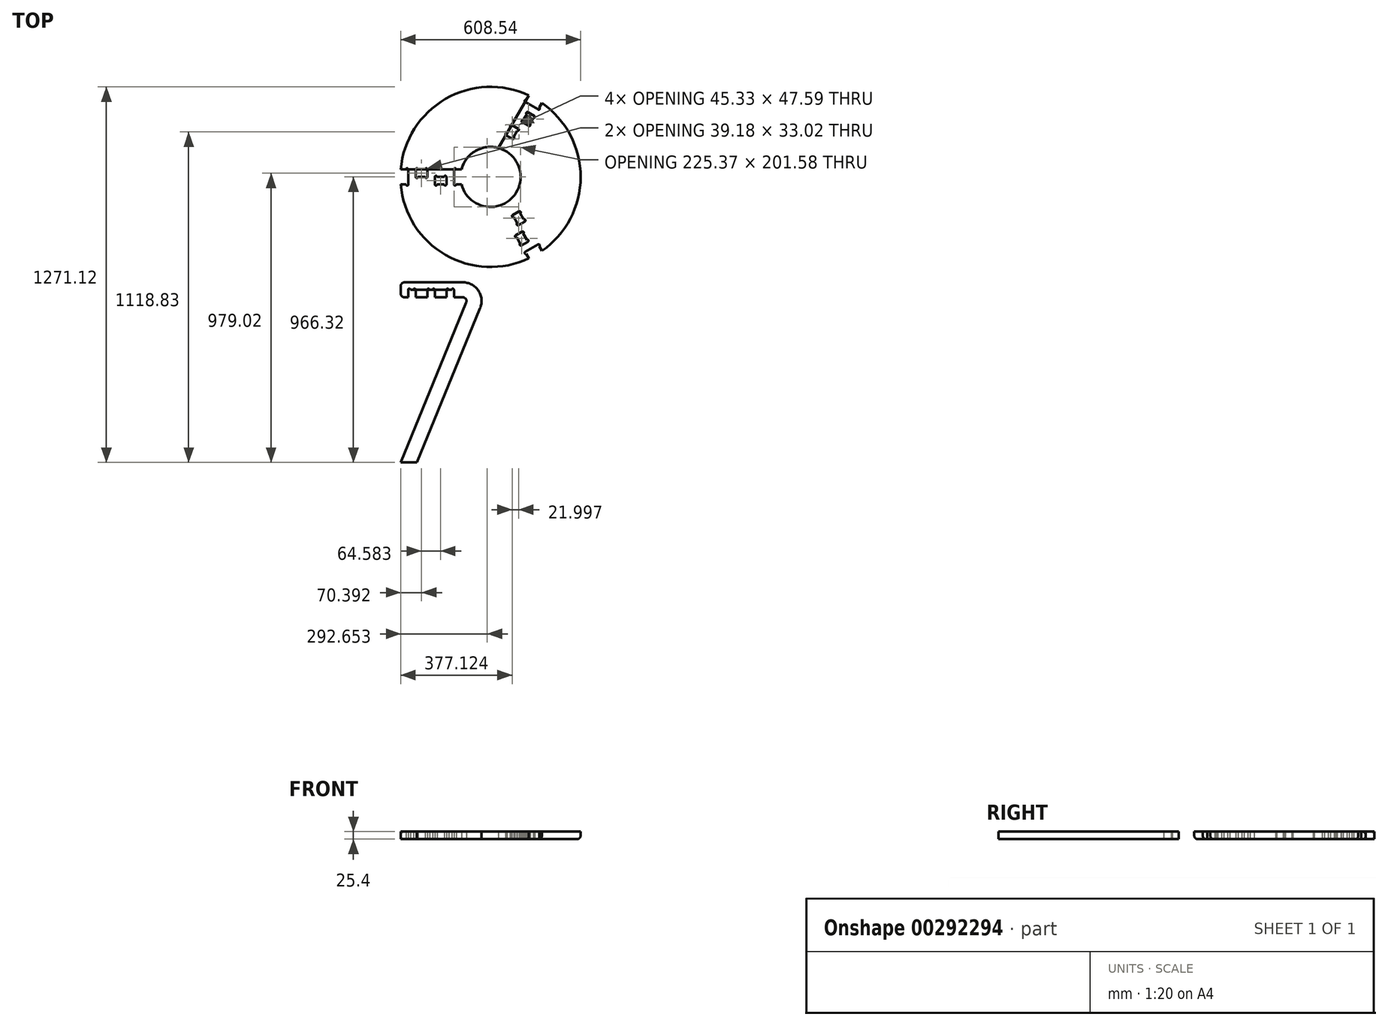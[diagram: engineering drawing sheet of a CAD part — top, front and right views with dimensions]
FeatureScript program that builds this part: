
annotation { "Feature Type Name" : "Feature", "Feature Type Description" : "" }
export const myFeature = defineFeature(function(context is Context, id is Id, definition is map)
    precondition{}
    {
        {
            assignVariable(context, id + "F0", {"name" : "t", "anyValue" : 25.4 * mm});
        }
        {
            var Q0;
            Q0=qCreatedBy(makeId("Top.planeOp"),FACE);
            var sketch = newSketch(context, id + "F1", { "sketchPlane" : qUnion([Q0])});
            skCircle(sketch, "E0", {"center": v(0, 0) * mm, "radius": 304.8 * mm});
            skCircle(sketch, "E1", {"center": v(0, 0) * mm, "radius": 25.4 * mm, "construction": true});
            skCircle(sketch, "E2", {"center": v(0, 0) * mm, "radius": 101.6 * mm});
            skLineSegment(sketch, "E3", {"start": v(0, 0) * mm, "end": v(-304.8, 0) * mm, "construction": true});
            skLineSegment(sketch, "E4", {"start": v(0, 0) * mm, "end": v(152.4, 263.96) * mm, "construction": true});
            skLineSegment(sketch, "E5", {"start": v(0, 0) * mm, "end": v(152.4, -263.96) * mm, "construction": true});
            skLineSegment(sketch, "E6", {"start": v(27.19, -97.9) * mm, "end": v(129.87, -275.75) * mm});
            skLineSegment(sketch, "E7", {"start": v(71.18, -72.5) * mm, "end": v(173.87, -250.35) * mm});
            skLineSegment(sketch, "E8", {"start": v(-303.74, 25.4) * mm, "end": v(-98.37, 25.4) * mm});
            skLineSegment(sketch, "E9", {"start": v(-303.74, -25.4) * mm, "end": v(-98.37, -25.4) * mm});
            skLineSegment(sketch, "E10", {"start": v(27.19, 97.9) * mm, "end": v(129.87, 275.75) * mm});
            skLineSegment(sketch, "E11", {"start": v(71.18, 72.5) * mm, "end": v(173.87, 250.35) * mm});
            skLineSegment(sketch, "E12", {"start": v(27.19, -97.9) * mm, "end": v(-71.18, 72.5) * mm, "construction": true});
            skSolve(sketch);
        }
        {
            var Q0;
            {var subQ0=sQuery(id+"F1.wireOp",EDGE,"E8");Q0=makeQuery(id+"F1.imprint","IMPRINT",FACE,{"disambiguationData":[TD([[makeQuery(id+"F1.imprint","IMPRINT",EDGE,{"derivedFrom":subQ0}),1.0]])]});}
            var sketch = newSketch(context, id + "F2", { "sketchPlane" : qUnion([Q0])});
            skPoint(sketch, "E13.0", {"position": v(0, 0) * mm});
            skPoint(sketch, "E14.0", {"position": v(-303.74, 25.4) * mm});
            skPoint(sketch, "E15.0", {"position": v(-303.74, -25.4) * mm});
            skPoint(sketch, "E16.0", {"position": v(173.87, -250.35) * mm});
            skPoint(sketch, "E17.0", {"position": v(173.87, 250.35) * mm});
            skPoint(sketch, "E18.0", {"position": v(129.87, 275.75) * mm});
            skPoint(sketch, "E19.0", {"position": v(27.19, 97.9) * mm});
            skPoint(sketch, "E20.0", {"position": v(-98.37, 25.4) * mm});
            skPoint(sketch, "E21.0", {"position": v(-98.37, -25.4) * mm});
            skPoint(sketch, "E22.0", {"position": v(27.19, -97.9) * mm});
            skPoint(sketch, "E23.0", {"position": v(71.18, -72.5) * mm});
            skLineSegment(sketch, "E24", {"start": v(-303.74, 25.4) * mm, "end": v(-98.37, 25.4) * mm});
            skLineSegment(sketch, "E25", {"start": v(-98.37, -25.4) * mm, "end": v(-303.74, -25.4) * mm});
            skPoint(sketch, "E26.0", {"position": v(71.18, 72.5) * mm});
            skLineSegment(sketch, "E27", {"start": v(-278.34, 25.4) * mm, "end": v(-278.34, -25.4) * mm});
            skLineSegment(sketch, "E28", {"start": v(-252.94, 25.4) * mm, "end": v(-252.94, 0) * mm});
            skLineSegment(sketch, "E29", {"start": v(-252.94, 0) * mm, "end": v(-213.76, 0) * mm});
            skLineSegment(sketch, "E30", {"start": v(-213.76, 0) * mm, "end": v(-213.76, 25.4) * mm});
            skLineSegment(sketch, "E31", {"start": v(-188.36, -25.4) * mm, "end": v(-188.36, 0) * mm});
            skLineSegment(sketch, "E32", {"start": v(-188.36, 0) * mm, "end": v(-149.17, 0) * mm});
            skLineSegment(sketch, "E33", {"start": v(-149.17, 0) * mm, "end": v(-149.17, -25.4) * mm});
            skCircle(sketch, "E34", {"center": v(0, 0) * mm, "radius": 304.8 * mm});
            skCircle(sketch, "E35", {"center": v(0, 0) * mm, "radius": 101.6 * mm});
            skPoint(sketch, "E36.1.5", {"position": v(129.87, -275.75) * mm});
            skArc(sketch, "E37", {"start": v(-278.34, 25.4) * mm, "mid": v(-282.15, 29.2) * mm, "end": v(-285.96, 25.4) * mm});
            skArc(sketch, "E38", {"start": v(-285.96, -25.4) * mm, "mid": v(-282.15, -29.21) * mm, "end": v(-278.34, -25.4) * mm});
            skArc(sketch, "E39", {"start": v(-252.94, 0) * mm, "mid": v(-249.13, -3.81) * mm, "end": v(-245.32, 0) * mm});
            skArc(sketch, "E40", {"start": v(-245.32, 25.4) * mm, "mid": v(-249.13, 29.2) * mm, "end": v(-252.94, 25.4) * mm});
            skArc(sketch, "E41", {"start": v(-213.76, 25.4) * mm, "mid": v(-217.57, 29.2) * mm, "end": v(-221.38, 25.4) * mm});
            skArc(sketch, "E42", {"start": v(-221.38, 0) * mm, "mid": v(-217.57, -3.81) * mm, "end": v(-213.76, 0) * mm});
            skArc(sketch, "E43", {"start": v(-180.74, 0) * mm, "mid": v(-184.55, 3.81) * mm, "end": v(-188.36, 0) * mm});
            skArc(sketch, "E44", {"start": v(-188.36, -25.4) * mm, "mid": v(-184.55, -29.21) * mm, "end": v(-180.74, -25.4) * mm});
            skArc(sketch, "E45", {"start": v(-149.17, 0) * mm, "mid": v(-152.98, 3.81) * mm, "end": v(-156.8, 0) * mm});
            skArc(sketch, "E46", {"start": v(-156.8, -25.4) * mm, "mid": v(-152.98, -29.21) * mm, "end": v(-149.17, -25.4) * mm});
            skLineSegment(sketch, "E47.1.0", {"start": v(129.87, -275.75) * mm, "end": v(27.19, -97.9) * mm});
            skLineSegment(sketch, "E47.1.1", {"start": v(117.17, -253.75) * mm, "end": v(161.17, -228.35) * mm});
            skLineSegment(sketch, "E47.1.2", {"start": v(94.18, -163.12) * mm, "end": v(74.59, -129.19) * mm});
            skLineSegment(sketch, "E47.1.4", {"start": v(71.18, -72.5) * mm, "end": v(173.87, -250.35) * mm});
            skLineSegment(sketch, "E47.1.7", {"start": v(126.47, -219.05) * mm, "end": v(106.88, -185.12) * mm});
            skLineSegment(sketch, "E47.1.8", {"start": v(74.59, -129.19) * mm, "end": v(96.58, -116.49) * mm});
            skLineSegment(sketch, "E47.1.10", {"start": v(116.18, -150.42) * mm, "end": v(94.18, -163.12) * mm});
            skLineSegment(sketch, "E47.1.11", {"start": v(106.88, -185.12) * mm, "end": v(84.88, -197.82) * mm});
            skLineSegment(sketch, "E47.1.12", {"start": v(104.47, -231.75) * mm, "end": v(126.47, -219.05) * mm});
            skArc(sketch, "E47.1.13", {"start": v(110.69, -191.72) * mm, "mid": v(112.08, -186.51) * mm, "end": v(106.88, -185.12) * mm});
            skArc(sketch, "E47.1.14", {"start": v(100.66, -225.15) * mm, "mid": v(99.27, -230.36) * mm, "end": v(104.47, -231.75) * mm});
            skArc(sketch, "E47.1.15", {"start": v(90.37, -156.52) * mm, "mid": v(88.97, -161.73) * mm, "end": v(94.18, -163.12) * mm});
            skArc(sketch, "E47.1.16", {"start": v(126.47, -219.05) * mm, "mid": v(127.86, -213.85) * mm, "end": v(122.66, -212.45) * mm});
            skArc(sketch, "E47.1.17", {"start": v(100.4, -123.09) * mm, "mid": v(101.79, -117.88) * mm, "end": v(96.58, -116.49) * mm});
            skArc(sketch, "E47.1.18", {"start": v(84.88, -197.82) * mm, "mid": v(83.49, -203.02) * mm, "end": v(88.7, -204.42) * mm});
            skArc(sketch, "E47.1.19", {"start": v(164.98, -234.95) * mm, "mid": v(166.37, -229.74) * mm, "end": v(161.17, -228.35) * mm});
            skArc(sketch, "E47.1.20", {"start": v(117.17, -253.75) * mm, "mid": v(115.78, -258.95) * mm, "end": v(120.98, -260.35) * mm});
            skArc(sketch, "E47.1.21", {"start": v(116.18, -150.42) * mm, "mid": v(117.57, -145.22) * mm, "end": v(112.37, -143.82) * mm});
            skArc(sketch, "E47.1.22", {"start": v(74.59, -129.19) * mm, "mid": v(73.2, -134.4) * mm, "end": v(78.4, -135.79) * mm});
            skLineSegment(sketch, "E47.2.0", {"start": v(173.87, 250.35) * mm, "end": v(71.18, 72.5) * mm});
            skLineSegment(sketch, "E47.2.1", {"start": v(161.17, 228.35) * mm, "end": v(117.17, 253.75) * mm});
            skLineSegment(sketch, "E47.2.2", {"start": v(94.18, 163.12) * mm, "end": v(74.59, 129.19) * mm});
            skLineSegment(sketch, "E47.2.4", {"start": v(27.19, 97.9) * mm, "end": v(129.87, 275.75) * mm});
            skLineSegment(sketch, "E47.2.7", {"start": v(126.47, 219.05) * mm, "end": v(106.88, 185.12) * mm});
            skLineSegment(sketch, "E47.2.8", {"start": v(74.59, 129.19) * mm, "end": v(52.59, 141.89) * mm});
            skLineSegment(sketch, "E47.2.10", {"start": v(72.18, 175.82) * mm, "end": v(94.18, 163.12) * mm});
            skLineSegment(sketch, "E47.2.11", {"start": v(106.88, 185.12) * mm, "end": v(128.88, 172.42) * mm});
            skLineSegment(sketch, "E47.2.12", {"start": v(148.47, 206.35) * mm, "end": v(126.47, 219.05) * mm});
            skArc(sketch, "E47.2.13", {"start": v(110.69, 191.72) * mm, "mid": v(105.48, 190.32) * mm, "end": v(106.88, 185.12) * mm});
            skArc(sketch, "E47.2.14", {"start": v(144.66, 199.75) * mm, "mid": v(149.86, 201.15) * mm, "end": v(148.47, 206.35) * mm});
            skArc(sketch, "E47.2.15", {"start": v(90.37, 156.52) * mm, "mid": v(95.57, 157.92) * mm, "end": v(94.18, 163.12) * mm});
            skArc(sketch, "E47.2.16", {"start": v(126.47, 219.05) * mm, "mid": v(121.27, 217.66) * mm, "end": v(122.66, 212.45) * mm});
            skArc(sketch, "E47.2.17", {"start": v(56.4, 148.49) * mm, "mid": v(51.2, 147.1) * mm, "end": v(52.59, 141.89) * mm});
            skArc(sketch, "E47.2.18", {"start": v(128.88, 172.42) * mm, "mid": v(134.08, 173.81) * mm, "end": v(132.69, 179.02) * mm});
            skArc(sketch, "E47.2.19", {"start": v(120.98, 260.35) * mm, "mid": v(115.78, 258.95) * mm, "end": v(117.17, 253.75) * mm});
            skArc(sketch, "E47.2.20", {"start": v(161.17, 228.35) * mm, "mid": v(166.37, 229.74) * mm, "end": v(164.98, 234.95) * mm});
            skArc(sketch, "E47.2.21", {"start": v(72.18, 175.82) * mm, "mid": v(66.98, 174.43) * mm, "end": v(68.37, 169.22) * mm});
            skArc(sketch, "E47.2.22", {"start": v(74.59, 129.19) * mm, "mid": v(79.8, 130.58) * mm, "end": v(78.4, 135.79) * mm});
            skLineSegment(sketch, "E48", {"start": v(-123.77, 25.4) * mm, "end": v(-123.77, -25.4) * mm});
            skArc(sketch, "E49", {"start": v(-116.15, 25.4) * mm, "mid": v(-119.96, 29.2) * mm, "end": v(-123.77, 25.4) * mm});
            skArc(sketch, "E50", {"start": v(-123.77, -25.4) * mm, "mid": v(-119.96, -29.21) * mm, "end": v(-116.15, -25.4) * mm});
            skSolve(sketch);
        }
        {
            var Q0;
            {var subQ0=sQuery(id+"F1.wireOp",EDGE,"E8");Q0=makeQuery(id+"F1.imprint","IMPRINT",FACE,{"disambiguationData":[TD([[makeQuery(id+"F1.imprint","IMPRINT",EDGE,{"derivedFrom":subQ0}),1.0]])]});}
            extrude(context, id + "F3", {"entities" : qUnion([Q0]), "depth" : getVariable(context, 't')});
        }
        {
            var Q0;
            {var subQ4=sQuery(id+"F2.wireOp",EDGE,"E38");Q0=makeQuery(id+"F2.imprint","IMPRINT",FACE,{"disambiguationData":[TD([[makeQuery(id+"F2.imprint","IMPRINT",EDGE,{"derivedFrom":subQ4}),-1.0]])]});}
            var Q1;
            {var subQ1=sQuery(id+"F2.wireOp",EDGE,"E47.1.17");Q1=makeQuery(id+"F2.imprint","IMPRINT",FACE,{"disambiguationData":[TD([[makeQuery(id+"F2.imprint","IMPRINT",EDGE,{"derivedFrom":subQ1}),-1.0]])]});}
            var Q2;
            {var subQ10=sQuery(id+"F2.wireOp",EDGE,"E37");Q2=makeQuery(id+"F2.imprint","IMPRINT",FACE,{"disambiguationData":[TD([[makeQuery(id+"F2.imprint","IMPRINT",EDGE,{"derivedFrom":subQ10}),-1.0]])]});}
            var Q3;
            {var subQ5=sQuery(id+"F2.wireOp",EDGE,"E27");Q3=makeQuery(id+"F2.imprint","IMPRINT",FACE,{"disambiguationData":[TD([[makeQuery(id+"F2.imprint","IMPRINT",EDGE,{"derivedFrom":subQ5}),1.0]])]});}
            var Q4;
            {var subQ11=sQuery(id+"F2.wireOp",EDGE,"E47.2.1");Q4=makeQuery(id+"F2.imprint","IMPRINT",FACE,{"disambiguationData":[TD([[makeQuery(id+"F2.imprint","IMPRINT",EDGE,{"derivedFrom":subQ11}),1.0]])]});}
            var Q5;
            {var subQ4=sQuery(id+"F2.wireOp",EDGE,"E47.1.1");Q5=makeQuery(id+"F2.imprint","IMPRINT",FACE,{"disambiguationData":[TD([[makeQuery(id+"F2.imprint","IMPRINT",EDGE,{"derivedFrom":subQ4}),1.0]])]});}
            extrude(context, id + "F4", {"entities" : qUnion([Q0, Q1, Q2, Q3, Q4, Q5]), "depth" : getVariable(context, 't')});
        }
        {
            var Q0;
            {var subQ1=sQuery(id+"F2.wireOp",EDGE,"E24");var subQ7=sQuery(id+"F2.wireOp",EDGE,"E34");var subQ10=makeQuery(id+"F2.imprint","INTERSECT",VERTEX,{"derivedFrom":[subQ1,subQ7]});Q0=makeQuery(id+"F2.imprint","IMPRINT",FACE,{"disambiguationData":[TD([[makeQuery(id+"F2.imprint","IMPRINT",EDGE,{"disambiguationData":[TD([[subQ10,-1.0]])],"derivedFrom":subQ1}),1.0]])]});}
            var sketch = newSketch(context, id + "F5", { "sketchPlane" : qUnion([Q0])});
            skLineSegment(sketch, "E51.bottom", {"start": v(-303.74, -356.72) * mm, "end": v(-93.77, -356.72) * mm});
            skLineSegment(sketch, "E51.top", {"start": v(-303.74, -966.32) * mm, "end": v(-248.84, -966.32) * mm});
            skLineSegment(sketch, "E51.left", {"start": v(-303.74, -356.72) * mm, "end": v(-303.74, -407.52) * mm});
            skPoint(sketch, "E52.0", {"position": v(-303.74, -25.4) * mm});
            skPoint(sketch, "E53.0", {"position": v(-278.34, -25.4) * mm});
            skPoint(sketch, "E54.0", {"position": v(-252.94, 0) * mm});
            skPoint(sketch, "E55.0", {"position": v(-213.76, 0) * mm});
            skPoint(sketch, "E56.0", {"position": v(-188.36, -25.4) * mm});
            skPoint(sketch, "E57.0", {"position": v(-149.17, -25.4) * mm});
            skPoint(sketch, "E58.0", {"position": v(-98.37, -25.4) * mm});
            skPoint(sketch, "E59.0", {"position": v(0, 0) * mm});
            skLineSegment(sketch, "E60", {"start": v(-303.74, -25.4) * mm, "end": v(-303.74, -356.72) * mm, "construction": true});
            skLineSegment(sketch, "E61", {"start": v(-303.74, -407.52) * mm, "end": v(-278.34, -407.52) * mm});
            skLineSegment(sketch, "E62", {"start": v(-303.74, -966.32) * mm, "end": v(-82.02, -425.03) * mm});
            skLineSegment(sketch, "E63", {"start": v(-248.84, -966.32) * mm, "end": v(-35.01, -444.29) * mm});
            skArc(sketch, "E64", {"start": v(-82.02, -425.03) * mm, "mid": v(-83.23, -413.14) * mm, "end": v(-93.77, -407.52) * mm});
            skArc(sketch, "E65", {"start": v(-93.77, -356.72) * mm, "mid": v(-41.05, -384.83) * mm, "end": v(-35.01, -444.29) * mm});
            skLineSegment(sketch, "E66", {"start": v(-303.74, -407.52) * mm, "end": v(-303.74, -966.32) * mm, "construction": true});
            skLineSegment(sketch, "E67", {"start": v(-278.34, -25.4) * mm, "end": v(-278.34, -382.12) * mm, "construction": true});
            skLineSegment(sketch, "E68", {"start": v(-252.94, 0) * mm, "end": v(-252.94, -382.12) * mm, "construction": true});
            skLineSegment(sketch, "E69", {"start": v(-213.76, 0) * mm, "end": v(-213.76, -382.12) * mm, "construction": true});
            skLineSegment(sketch, "E70", {"start": v(-188.36, -25.4) * mm, "end": v(-188.36, -382.12) * mm, "construction": true});
            skLineSegment(sketch, "E71", {"start": v(-149.17, -25.4) * mm, "end": v(-149.17, -382.12) * mm, "construction": true});
            skLineSegment(sketch, "E72", {"start": v(-303.74, -382.12) * mm, "end": v(-278.34, -382.12) * mm, "construction": true});
            skLineSegment(sketch, "E73", {"start": v(-278.34, -382.12) * mm, "end": v(-278.34, -407.52) * mm});
            skLineSegment(sketch, "E74", {"start": v(-278.34, -382.12) * mm, "end": v(-252.94, -382.12) * mm});
            skLineSegment(sketch, "E75", {"start": v(-252.94, -382.12) * mm, "end": v(-213.76, -382.12) * mm});
            skLineSegment(sketch, "E76", {"start": v(-252.94, -382.12) * mm, "end": v(-252.94, -407.52) * mm});
            skLineSegment(sketch, "E77", {"start": v(-278.34, -407.52) * mm, "end": v(-252.94, -407.52) * mm});
            skLineSegment(sketch, "E78", {"start": v(-252.94, -407.52) * mm, "end": v(-213.76, -407.52) * mm});
            skLineSegment(sketch, "E79", {"start": v(-213.76, -407.52) * mm, "end": v(-188.36, -407.52) * mm});
            skLineSegment(sketch, "E80", {"start": v(-188.36, -407.52) * mm, "end": v(-188.36, -407.52) * mm});
            skLineSegment(sketch, "E81", {"start": v(-213.76, -407.52) * mm, "end": v(-213.76, -407.52) * mm});
            skLineSegment(sketch, "E82", {"start": v(-213.76, -382.12) * mm, "end": v(-213.76, -407.52) * mm});
            skLineSegment(sketch, "E83", {"start": v(-213.76, -382.12) * mm, "end": v(-188.36, -382.12) * mm});
            skLineSegment(sketch, "E84", {"start": v(-188.36, -382.12) * mm, "end": v(-149.17, -382.12) * mm});
            skLineSegment(sketch, "E85", {"start": v(-188.36, -382.12) * mm, "end": v(-188.36, -407.52) * mm});
            skLineSegment(sketch, "E86", {"start": v(-149.17, -382.12) * mm, "end": v(-149.17, -407.52) * mm});
            skLineSegment(sketch, "E87", {"start": v(-149.17, -382.12) * mm, "end": v(-123.77, -382.12) * mm});
            skLineSegment(sketch, "E88", {"start": v(-123.77, -382.12) * mm, "end": v(-42.97, -382.12) * mm, "construction": true});
            skLineSegment(sketch, "E89", {"start": v(0, 0) * mm, "end": v(0, -960.78) * mm, "construction": true});
            skLineSegment(sketch, "E90", {"start": v(-30.27, 20) * mm, "end": v(-30.27, -420.22) * mm, "construction": true});
            skLineSegment(sketch, "E91", {"start": v(-98.37, -25.4) * mm, "end": v(-30.27, -25.4) * mm, "construction": true});
            skLineSegment(sketch, "E92", {"start": v(-149.17, -407.52) * mm, "end": v(-188.36, -407.52) * mm});
            skLineSegment(sketch, "E93", {"start": v(-123.77, -382.12) * mm, "end": v(-123.77, -407.52) * mm});
            skLineSegment(sketch, "E94", {"start": v(-93.77, -407.52) * mm, "end": v(-123.77, -407.52) * mm});
            skLineSegment(sketch, "E95", {"start": v(-123.77, -407.52) * mm, "end": v(-149.17, -407.52) * mm});
            skArc(sketch, "E96", {"start": v(-270.72, -382.12) * mm, "mid": v(-274.53, -378.3) * mm, "end": v(-278.34, -382.12) * mm});
            skArc(sketch, "E97", {"start": v(-188.36, -382.12) * mm, "mid": v(-192.17, -378.3) * mm, "end": v(-195.98, -382.12) * mm});
            skArc(sketch, "E98", {"start": v(-141.55, -382.12) * mm, "mid": v(-145.36, -378.3) * mm, "end": v(-149.17, -382.12) * mm});
            skArc(sketch, "E99", {"start": v(-123.77, -382.12) * mm, "mid": v(-127.58, -378.3) * mm, "end": v(-131.4, -382.12) * mm});
            skArc(sketch, "E100", {"start": v(-206.14, -382.12) * mm, "mid": v(-209.95, -378.3) * mm, "end": v(-213.76, -382.12) * mm});
            skArc(sketch, "E101", {"start": v(-252.94, -382.12) * mm, "mid": v(-256.75, -378.3) * mm, "end": v(-260.56, -382.12) * mm});
            skLineSegment(sketch, "E102", {"start": v(-98.37, -25.4) * mm, "end": v(-98.37, -407.52) * mm, "construction": true});
            skPoint(sketch, "E103.0", {"position": v(71.18, 72.5) * mm});
            skPoint(sketch, "E104.0", {"position": v(27.19, 97.9) * mm});
            skPoint(sketch, "E105.0", {"position": v(-98.37, 25.4) * mm});
            skPoint(sketch, "E106.0", {"position": v(71.18, -72.5) * mm});
            skPoint(sketch, "E107.0", {"position": v(27.19, -97.9) * mm});
            skPoint(sketch, "E108.0", {"position": v(-123.77, -25.4) * mm});
            skLineSegment(sketch, "E109", {"start": v(-123.77, -25.4) * mm, "end": v(-123.77, -382.12) * mm, "construction": true});
            skSolve(sketch);
        }
        {
            var Q0;
            Q0=makeQuery(id+"F5.imprint","IMPRINT",FACE,{"disambiguationData":[TD([[makeQuery(id+"F5.imprint","IMPRINT",EDGE,{"derivedFrom":sQuery(id+"F5.wireOp",EDGE,"E51.bottom")}),-1.0]])]});
            var Q1;
            Q1=makeQuery(id+"F5.imprint","IMPRINT",FACE,{"disambiguationData":[TD([[makeQuery(id+"F5.imprint","IMPRINT",EDGE,{"derivedFrom":sQuery(id+"F5.wireOp",EDGE,"E84")}),-1.0]])]});
            var Q2;
            {var subQ0=sQuery(id+"F5.wireOp",EDGE,"E101");Q2=makeQuery(id+"F5.imprint","IMPRINT",FACE,{"disambiguationData":[TD([[makeQuery(id+"F5.imprint","IMPRINT",EDGE,{"derivedFrom":subQ0}),1.0]])]});}
            var Q3;
            {var subQ0=sQuery(id+"F5.wireOp",EDGE,"E100");Q3=makeQuery(id+"F5.imprint","IMPRINT",FACE,{"disambiguationData":[TD([[makeQuery(id+"F5.imprint","IMPRINT",EDGE,{"derivedFrom":subQ0}),1.0]])]});}
            extrude(context, id + "F6", {"entities" : qUnion([Q0, Q1, Q2, Q3]), "depth" : getVariable(context, 't')});
        }
        {
            var Q0;
            Q0=makeQuery(id+"F5.imprint","IMPRINT",FACE,{"disambiguationData":[TD([[makeQuery(id+"F5.imprint","IMPRINT",EDGE,{"derivedFrom":sQuery(id+"F5.wireOp",EDGE,"E51.bottom")}),-1.0]])]});
            var Q1;
            Q1=makeQuery(id+"F5.imprint","IMPRINT",FACE,{"disambiguationData":[TD([[makeQuery(id+"F5.imprint","IMPRINT",EDGE,{"derivedFrom":sQuery(id+"F5.wireOp",EDGE,"E75")}),-1.0]])]});
            var Q2;
            {var subQ0=sQuery(id+"F5.wireOp",EDGE,"E97");Q2=makeQuery(id+"F5.imprint","IMPRINT",FACE,{"disambiguationData":[TD([[makeQuery(id+"F5.imprint","IMPRINT",EDGE,{"derivedFrom":subQ0}),1.0]])]});}
            var Q3;
            {var subQ0=sQuery(id+"F5.wireOp",EDGE,"E98");Q3=makeQuery(id+"F5.imprint","IMPRINT",FACE,{"disambiguationData":[TD([[makeQuery(id+"F5.imprint","IMPRINT",EDGE,{"derivedFrom":subQ0}),1.0]])]});}
            extrude(context, id + "F7", {"entities" : qUnion([Q0, Q1, Q2, Q3]), "depth" : getVariable(context, 't')});
        }
        {
            var Q0;
            Q0=makeQuery(id+"F6.opExtrude","SWEPT_EDGE",EDGE,{"disambiguationData":[OSD([sQuery(id+"F5.wireOp",EDGE,"E51.bottom"),sQuery(id+"F5.wireOp",EDGE,"E51.left")])]});
            var Q1;
            Q1=makeQuery(id+"F6.opExtrude","SWEPT_EDGE",EDGE,{"disambiguationData":[OSD([sQuery(id+"F5.wireOp",EDGE,"E51.left"),sQuery(id+"F5.wireOp",EDGE,"E61")])]});
            fillet(context, id + "F8", {"entities" : qUnion([Q0, Q1]), "radius" : 12.7 * mm, "tangentPropagation" : true, "allowEdgeOverflow" : false});
        }
        {
            var Q0;
            Q0=makeQuery(id+"F7.opExtrude","SWEPT_EDGE",EDGE,{"disambiguationData":[OSD([sQuery(id+"F5.wireOp",EDGE,"E51.bottom"),sQuery(id+"F5.wireOp",EDGE,"E51.left")])]});
            var Q1;
            Q1=makeQuery(id+"F7.opExtrude","SWEPT_EDGE",EDGE,{"disambiguationData":[OSD([sQuery(id+"F5.wireOp",EDGE,"E51.left"),sQuery(id+"F5.wireOp",EDGE,"E61")])]});
            fillet(context, id + "F9", {"entities" : qUnion([Q0, Q1]), "radius" : 12.7 * mm, "tangentPropagation" : true, "allowEdgeOverflow" : false});
        }
        {
            var Q0;
            Q0=makeQuery(id+"F3.opExtrude","CAP_EDGE",EDGE,{"disambiguationData":[OSD([sQuery(id+"F1.wireOp",EDGE,"E0")])],"isStart":false});
            fillet(context, id + "F10", {"entities" : qUnion([Q0]), "radius" : 12.7 * mm, "tangentPropagation" : true, "allowEdgeOverflow" : false});
        }
        {
            var Q0;
            {var subQ0=sQuery(id+"F2.wireOp",EDGE,"E34");Q0=makeQuery(id+"F4.opExtrude","CAP_EDGE",EDGE,{"disambiguationData":[OSD([subQ0]),TDD([makeQuery(id+"F2.imprint","IMPRINT",EDGE,{"disambiguationData":[TD([[makeQuery(id+"F2.imprint","INTERSECT",VERTEX,{"derivedFrom":[sQuery(id+"F2.wireOp",EDGE,"E24"),subQ0]}),1.0]])],"derivedFrom":subQ0})])],"isStart":true});}
            var Q1;
            {var subQ0=sQuery(id+"F2.wireOp",EDGE,"E34");Q1=makeQuery(id+"F4.opExtrude","CAP_EDGE",EDGE,{"disambiguationData":[OSD([subQ0]),TDD([makeQuery(id+"F2.imprint","IMPRINT",EDGE,{"disambiguationData":[TD([[makeQuery(id+"F2.imprint","INTERSECT",VERTEX,{"derivedFrom":[sQuery(id+"F2.wireOp",EDGE,"E25"),subQ0]}),-1.0]])],"derivedFrom":subQ0})])],"isStart":true});}
            var Q2;
            {var subQ0=sQuery(id+"F2.wireOp",EDGE,"E34");Q2=makeQuery(id+"F4.opExtrude","CAP_EDGE",EDGE,{"disambiguationData":[OSD([subQ0]),TDD([makeQuery(id+"F2.imprint","IMPRINT",EDGE,{"disambiguationData":[TD([[makeQuery(id+"F2.imprint","INTERSECT",VERTEX,{"derivedFrom":[subQ0,sQuery(id+"F2.wireOp",EDGE,"E36.1.12")]}),-1.0]])],"derivedFrom":subQ0})])],"isStart":true});}
            fillet(context, id + "F11", {"entities" : qUnion([Q0, Q1, Q2]), "radius" : 12.7 * mm, "tangentPropagation" : true, "allowEdgeOverflow" : false});
        }
    });
